# Revit family: Hager-IC-IP40-Plain_Door_1Row-syst-PL-pl
name_source: partatom
category: Electrical Equipment
units: mm (PartAtom-declared; Revit-internal decimal feet)

## family parameters
Cut with Voids When Loaded = No
Host = Face
Panel Configuration = Two Columns, Circuits Across
Part Type = Panelboard
Room Calculation Point = No
Round Connector Dimension = Use Diameter
Shared = No

## types (8) — shared parameters
Classification.Uniclass.Pr.Description = Control circuit device enclosures
Classification.Uniclass.Pr.Number = Pr_80_77_28_16
EF000007 - Kolor = EV000202 - Biały
EF000049 - Głębokość = 91 mm  [stored 0.298556 ft]
EF000116 - Numer RAL = 9010
EF000118 - Z płytą montażową = No
EF000266 - Liczba rzędów = 1
EF000339 - Rodzaj pokrywy = EV004216 - Drzwi
EF001062 - Wykonane zgodnie z Dyrektywą Kompatybilności Elektromagnetycznej EMC = No
EF001088 - Możliwość rozbudowy = Yes
EF001131 - Głębokość wewnętrzna = 72 mm  [stored 0.23622 ft]
EF001134 - Szyna DIN = Yes
EF001596 - Materiał obudowy = EV000139 - Tworzywo sztuczne
EF004462 - Rodzaj zamknięcia = EV000154 - Inne
EF005474 - Stopień ochrony (IP) = EV006415 - IP40
EF006244 - Transparentna pokrywa/drzwi = No
EF006306 - Z zamkiem = No
EF009212 - Wykonanie pokrywy = EV000116 - Zamknięty
EF015776 - Listwa zaciskowa uziemienia = Yes
EF015777 - Listwa zaciskowa przewodu neutralnego = Yes
EF015941 - Drzwi przepuszczające sygnał = Yes
Ground Bus = No
HG000002 - Z drzwiami lub pokrywą = Yes
HG000003 - Zakres = IC
HG000005 - Grubość = 3 mm  [stored 0.00984252 ft]
HG000017 - Odległość między biegunami = 18 mm  [stored 0.0590551 ft]
Manufacturer = Hager
Neutral Bus = No
Type Comments = IC
zero-valued in all types: Default Elevation

## per-type parameters (varying)
| type | EF000003 - Sposób montażu | EF000008 - Szerokość | EF000040 - Wysokość | EF000218 - Głębokość wbudowania | EF000332 - Wysokość wbudowania | EF000846 - Szerokość wbudowania | EF002950 - Szerokość wyrażona liczbą modułów | HG000004 - Referencja producenta | HG000006 - Montaż podtynkowy | Model |
| Montaż natynkowy IP40 S134.5 W170 G91 6 Jednostki dywizyjne - VD106PP | EV000384 - Montaż natynkowy | 134 mm | 170 mm  [stored 0.557743 ft] | 0 mm  [stored 0 ft] | 0 mm  [stored 0 ft] | 0 mm  [stored 0 ft] | 6 | VD106PP | No | VD106PP |
| Montaż natynkowy IP40 S170.5 W170 G91 8 Jednostki dywizyjne - VD108PP | EV000384 - Montaż natynkowy | 170 mm  [stored 0.557743 ft] | 170 mm  [stored 0.557743 ft] | 0 mm  [stored 0 ft] | 0 mm  [stored 0 ft] | 0 mm  [stored 0 ft] | 8 | VD108PP | No | VD108PP |
| Montaż natynkowy IP40 S206.5 W170 G91 10 Jednostki dywizyjne - VD110PP | EV000384 - Montaż natynkowy | 206 mm  [stored 0.675853 ft] | 170 mm  [stored 0.557743 ft] | 0 mm  [stored 0 ft] | 0 mm  [stored 0 ft] | 0 mm  [stored 0 ft] | 10 | VD110PP | No | VD110PP |
| Montaż natynkowy IP40 S292.5 W200 G91 12 Jednostki dywizyjne - VD112PP | EV000384 - Montaż natynkowy | 292 mm  [stored 0.958005 ft] | 200 mm  [stored 0.656168 ft] | 0 mm  [stored 0 ft] | 0 mm  [stored 0 ft] | 0 mm  [stored 0 ft] | 12 | VD112PP | No | VD112PP |
| Montaż natynkowy IP40 S400 W200 G91 18 Jednostki dywizyjne - VD118PP | EV000384 - Montaż natynkowy | 400 mm  [stored 1.31234 ft] | 200 mm  [stored 0.656168 ft] | 0 mm  [stored 0 ft] | 0 mm  [stored 0 ft] | 0 mm  [stored 0 ft] | 18 | VD118PP | No | VD118PP |
| Montaż podtynkowy IP40 S236 W206 G91.4 8 Jednostki dywizyjne - VR108PP | EV000383 - Montaż podtynkowy | 236 mm | 206 mm  [stored 0.675853 ft] | 72 mm  [stored 0.23622 ft] | 188 mm  [stored 0.616798 ft] | 218 mm  [stored 0.715223 ft] | 8 | VR108PP | Yes | VR108PP |
| Montaż podtynkowy IP40 S308 W226 G91.4 12 Jednostki dywizyjne - VR112PP | EV000383 - Montaż podtynkowy | 308 mm  [stored 1.0105 ft] | 226 mm  [stored 0.74147 ft] | 72 mm  [stored 0.23622 ft] | 208 mm | 290 mm  [stored 0.951444 ft] | 12 | VR112PP | Yes | VR112PP |
| Montaż podtynkowy IP40 S416 W226 G91.4 18 Jednostki dywizyjne - VR118PP | EV000383 - Montaż podtynkowy | 416 mm | 226 mm  [stored 0.74147 ft] | 72 mm  [stored 0.23622 ft] | 208 mm | 398 mm  [stored 1.30577 ft] | 18 | VR118PP | Yes | VR118PP |

note: [stored X ft] marks values corroborated as IEEE doubles in the binary element streams (Revit-internal decimal feet)

## geometry (parser evidence)
native form markers: Blend x4, Sweep x12
no freeform markers — native parametric forms only
